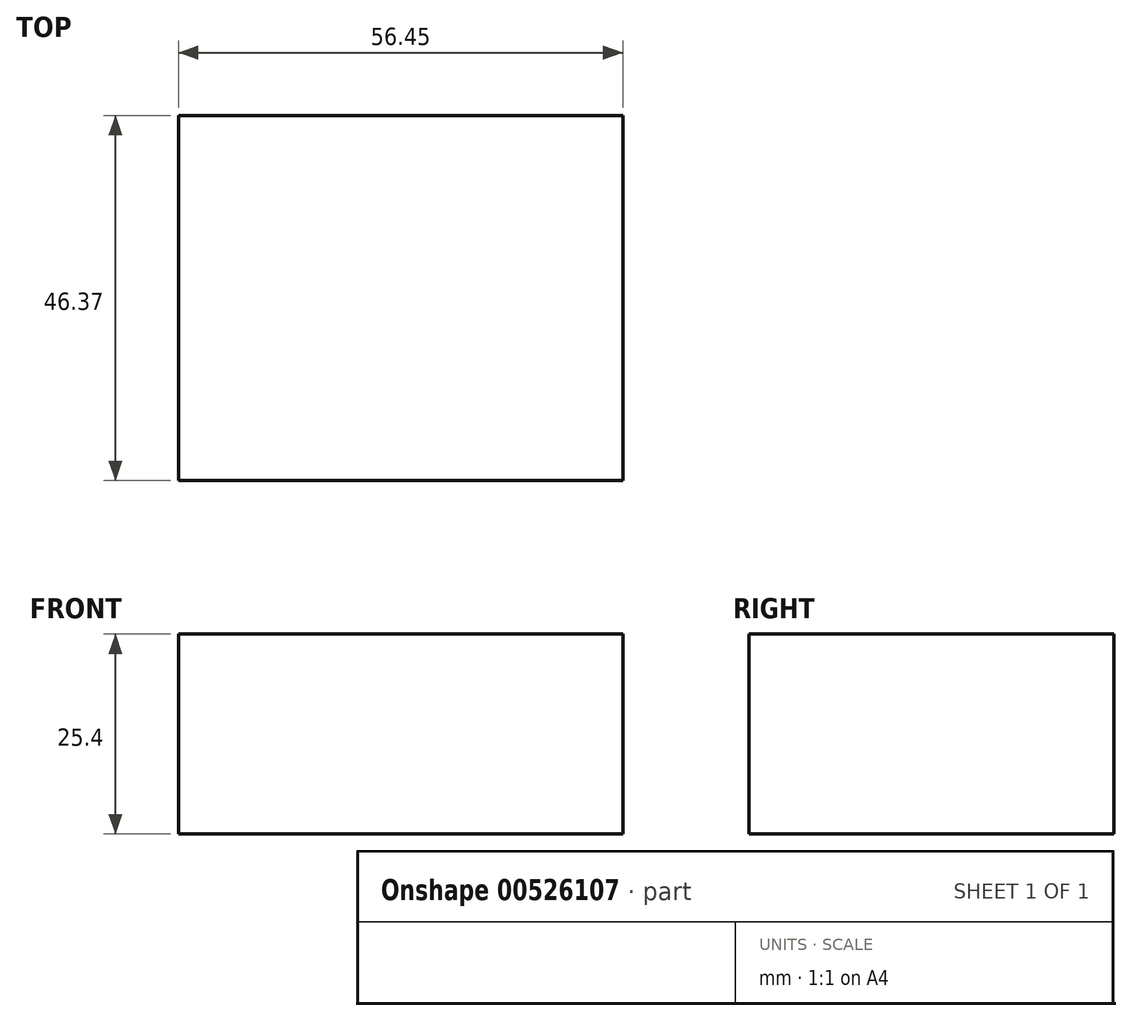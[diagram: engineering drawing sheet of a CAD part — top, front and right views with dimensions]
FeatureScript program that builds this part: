
annotation { "Feature Type Name" : "Feature", "Feature Type Description" : "" }
export const myFeature = defineFeature(function(context is Context, id is Id, definition is map)
    precondition{}
    {
        {
            var Q0;
            Q0=qCreatedBy(makeId("Top.planeOp"),FACE);
            var sketch = newSketch(context, id + "F0", { "sketchPlane" : qUnion([Q0])});
            skLineSegment(sketch, "E0.bottom", {"start": v(-49.08, 29.12) * mm, "end": v(7.37, 29.12) * mm});
            skLineSegment(sketch, "E0.top", {"start": v(-49.08, -17.25) * mm, "end": v(7.37, -17.25) * mm});
            skLineSegment(sketch, "E0.left", {"start": v(-49.08, 29.12) * mm, "end": v(-49.08, -17.25) * mm});
            skLineSegment(sketch, "E0.right", {"start": v(7.37, 29.12) * mm, "end": v(7.37, -17.25) * mm});
            skSolve(sketch);
        }
        {
            var Q0;
            Q0=makeQuery(id+"F0.imprint","IMPRINT",FACE,{"disambiguationData":[TD([[makeQuery(id+"F0.imprint","IMPRINT",EDGE,{"derivedFrom":sQuery(id+"F0.wireOp",EDGE,"E0.bottom")}),-1.0]])]});
            extrude(context, id + "F1", {"entities" : qUnion([Q0]), "depth" : 25.4 * mm, "offsetDistance" : 25.4 * mm});
        }
        {
            var Q0;
            Q0=makeQuery(id+"F1.opExtrude","CAP_FACE",FACE,{"disambiguationData":[OSD([sQuery(id+"F0.wireOp",EDGE,"E0.bottom"),sQuery(id+"F0.wireOp",EDGE,"E0.top"),sQuery(id+"F0.wireOp",EDGE,"E0.left"),sQuery(id+"F0.wireOp",EDGE,"E0.right")])],"isStart":false});
            var sketch = newSketch(context, id + "F2", { "sketchPlane" : qUnion([Q0])});
            skCircle(sketch, "E1", {"center": v(-23.67, 5.86) * mm, "radius": 10.42 * mm});
            skSolve(sketch);
        }
        {
            var Q0;
            Q0=makeQuery(id+"F2.imprint","IMPRINT",FACE,{"disambiguationData":[TD([[makeQuery(id+"F2.imprint","IMPRINT",EDGE,{"derivedFrom":sQuery(id+"F2.wireOp",EDGE,"E1")}),1.0]])]});
            extrude(context, id + "F3", {"entities" : qUnion([Q0]), "endBound" : BoundingType.SYMMETRIC, "depth" : 25.4 * mm, "offsetDistance" : 25.4 * mm});
        }
        {
            var Q0;
            Q0=makeQuery(id+"F3.opExtrude","SWEPT_BODY",BODY,{"disambiguationData":[OSD([sQuery(id+"F2.wireOp",EDGE,"E1")])]});
            deleteBodies(context, id + "F4", {"entities" : qUnion([Q0])});
        }
    });
